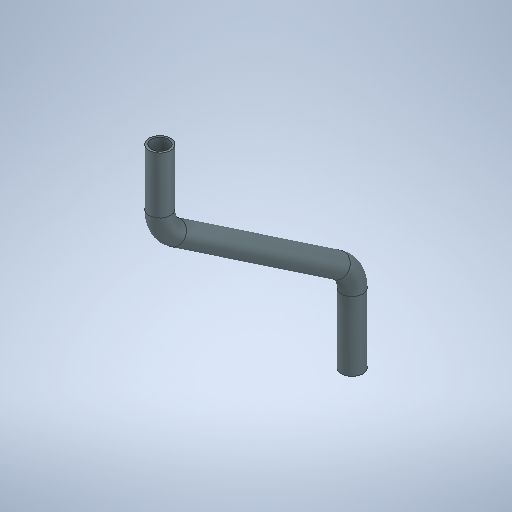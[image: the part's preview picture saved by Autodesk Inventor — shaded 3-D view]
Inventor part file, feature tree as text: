
AUTODESK INVENTOR PART (.ipt)
format: ipt  version: 2025.1 (Build 291241000, 241)  size: 285,184 bytes
history: native  units: mm
features: sketch x2, sweep x1, shell x1
ambient origin geometry x8: Origin, YZ Plane, XZ Plane, XY Plane, X Axis, Y Axis, Z Axis, Center Point
bodies: Solid1 (feature_tree)
feature tree (4):
  sweep  "Sweep1"
  shell  "Shell1"  Thickness=30.0mm
  sketch  "Sketch1"  dims[d0=5.0mm d1=17.0mm d2=30.0mm]
  sketch  "Sketch3"  dims[d3=44.5mm d4=20.0mm d5=7.5mm d6=0.0mm d7=0.0mm d8=0.5mm]
